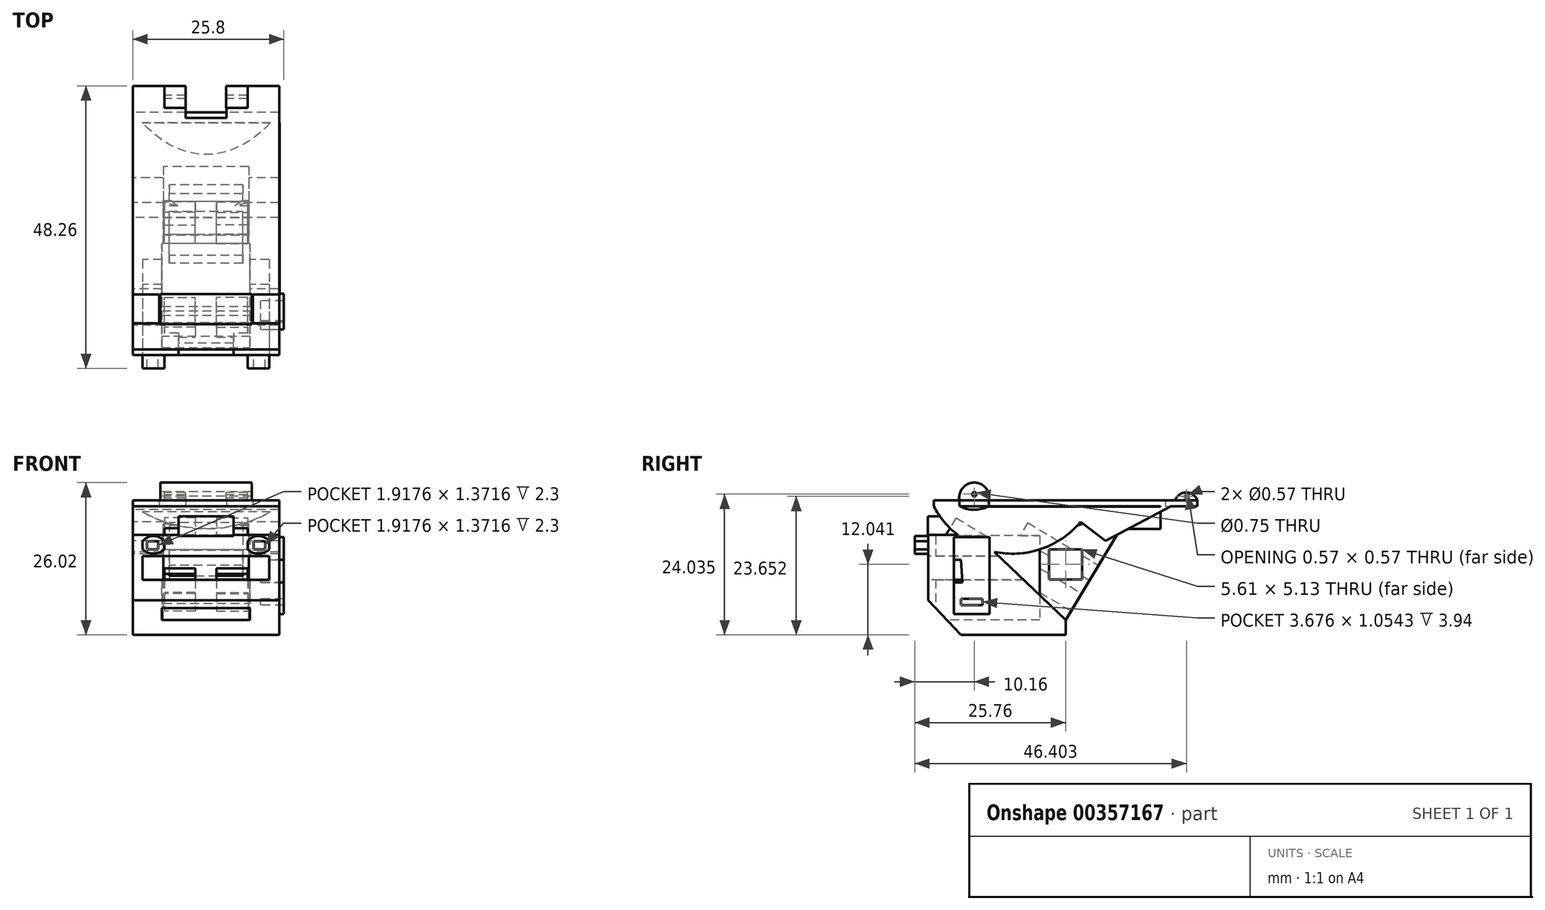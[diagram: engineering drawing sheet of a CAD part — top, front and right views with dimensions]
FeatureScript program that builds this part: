
annotation { "Feature Type Name" : "Feature", "Feature Type Description" : "" }
export const myFeature = defineFeature(function(context is Context, id is Id, definition is map)
    precondition{}
    {
        {
            var Q0;
            Q0=qCreatedBy(makeId("Top.planeOp"),FACE);
            var sketch = newSketch(context, id + "F0", { "sketchPlane" : qUnion([Q0])});
            skLineSegment(sketch, "E0.bottom", {"start": v(12.5, -22.5) * mm, "end": v(-12.5, -22.5) * mm});
            skLineSegment(sketch, "E0.top", {"start": v(12.5, 22.5) * mm, "end": v(3.5, 22.5) * mm});
            skLineSegment(sketch, "E0.left", {"start": v(12.5, -22.5) * mm, "end": v(12.5, -18.1) * mm});
            skLineSegment(sketch, "E0.right", {"start": v(-12.5, -22.5) * mm, "end": v(-12.5, -18.1) * mm});
            skPoint(sketch, "E0.middle", {"position": v(0, 0) * mm});
            skLineSegment(sketch, "E1.MirrorCS", {"start": v(-12.5, -13.1) * mm, "end": v(-8, -13.1) * mm});
            skLineSegment(sketch, "E2.MirrorCS", {"start": v(-8, -13.1) * mm, "end": v(-8, -18.1) * mm});
            skLineSegment(sketch, "E3.MirrorCS", {"start": v(-12.5, -18.1) * mm, "end": v(-8, -18.1) * mm});
            skLineSegment(sketch, "E4.MirrorCS", {"start": v(12.5, -18.1) * mm, "end": v(8, -18.1) * mm});
            skLineSegment(sketch, "E5.MirrorCS", {"start": v(12.5, -13.1) * mm, "end": v(8, -13.1) * mm});
            skLineSegment(sketch, "E6.MirrorCS", {"start": v(8, -13.1) * mm, "end": v(8, -18.1) * mm});
            skLineSegment(sketch, "E7.trimOffspring", {"start": v(-12.5, 18.1) * mm, "end": v(-12.5, 22.5) * mm});
            skLineSegment(sketch, "E8.trimOffspring", {"start": v(12.5, 18.1) * mm, "end": v(12.5, 22.5) * mm});
            skLineSegment(sketch, "E9.trimOffspring", {"start": v(12.5, -13.1) * mm, "end": v(12.5, 13.1) * mm});
            skLineSegment(sketch, "E10.trimOffspring", {"start": v(-12.5, -13.1) * mm, "end": v(-12.5, 13.1) * mm});
            skLineSegment(sketch, "E11", {"start": v(-12.5, 18.1) * mm, "end": v(-12.5, 13.1) * mm});
            skLineSegment(sketch, "E12", {"start": v(12.5, 18.1) * mm, "end": v(12.5, 13.1) * mm});
            skLineSegment(sketch, "E13.bottom", {"start": v(3.5, 17.07) * mm, "end": v(-3.5, 17.07) * mm});
            skLineSegment(sketch, "E13.left", {"start": v(3.5, 17.07) * mm, "end": v(3.5, 22.5) * mm});
            skLineSegment(sketch, "E13.right", {"start": v(-3.5, 17.07) * mm, "end": v(-3.5, 22.5) * mm});
            skPoint(sketch, "E13.middle", {"position": v(0, 22.5) * mm});
            skPoint(sketch, "E14.orphan", {"position": v(-3.5, 27.93) * mm});
            skPoint(sketch, "E15.orphan", {"position": v(3.5, 27.93) * mm});
            skLineSegment(sketch, "E16.trimOffspring", {"start": v(-3.5, 22.5) * mm, "end": v(-12.5, 22.5) * mm});
            skSolve(sketch);
        }
        {
            var Q0;
            Q0 = qSketchRegion(id + "F0", true);
            extrude(context, id + "F1", {"entities" : qUnion([Q0]), "depth" : 1 * mm});
        }
        {
            var Q0;
            Q0=qCreatedBy(makeId("Right.planeOp"),FACE);
            var sketch = newSketch(context, id + "F2", { "sketchPlane" : qUnion([Q0])});
            skCircle(sketch, "E17", {"center": v(-15.6, 2.05) * mm, "radius": 0.38 * mm});
            skLineSegment(sketch, "E18", {"start": v(-18.13, 1) * mm, "end": v(-13.1, 0.97) * mm});
            skArc(sketch, "E19", {"start": v(-13.1, 0.97) * mm, "mid": v(-15.59, 4.04) * mm, "end": v(-18.13, 1) * mm});
            skSolve(sketch);
        }
        {
            var Q0;
            Q0 = qSketchRegion(id + "F2", true);
            extrude(context, id + "F3", {"entities" : qUnion([Q0]), "operationType" : NewBodyOperationType.ADD, "endBound" : BoundingType.SYMMETRIC, "depth" : 15.6 * mm});
        }
        {
            var Q0;
            Q0=qCreatedBy(makeId("Right.planeOp"),FACE);
            var sketch = newSketch(context, id + "F4", { "sketchPlane" : qUnion([Q0])});
            skArc(sketch, "E20", {"start": v(22.5, 1) * mm, "mid": v(20.61, 2.34) * mm, "end": v(18.73, 1) * mm});
            skLineSegment(sketch, "E21", {"start": v(22.5, 1) * mm, "end": v(18.73, 1) * mm});
            skCircle(sketch, "E22", {"center": v(20.64, 1.67) * mm, "radius": 0.28 * mm});
            skSolve(sketch);
        }
        {
            var Q0;
            Q0 = qSketchRegion(id + "F4", true);
            extrude(context, id + "F5", {"entities" : qUnion([Q0]), "endBound" : BoundingType.SYMMETRIC, "depth" : 14.2 * mm});
        }
        {
            var Q0;
            Q0=makeQuery(id+"F5.opExtrude","SWEPT_FACE",FACE,{"disambiguationData":[OSD([sQuery(id+"F4.wireOp",EDGE,"E21")])]});
            var sketch = newSketch(context, id + "F6", { "sketchPlane" : qUnion([Q0])});
            skLineSegment(sketch, "E23.bottom", {"start": v(-3.5, -18.73) * mm, "end": v(3.46, -18.73) * mm});
            skLineSegment(sketch, "E23.top", {"start": v(-3.5, -22.5) * mm, "end": v(3.46, -22.5) * mm});
            skLineSegment(sketch, "E23.left", {"start": v(-3.5, -18.73) * mm, "end": v(-3.5, -22.5) * mm});
            skLineSegment(sketch, "E23.right", {"start": v(3.46, -18.73) * mm, "end": v(3.46, -22.5) * mm});
            skSolve(sketch);
        }
        {
            var Q0;
            Q0=makeQuery(id+"F6.imprint","IMPRINT",FACE,{"disambiguationData":[TD([[makeQuery(id+"F6.imprint","IMPRINT",EDGE,{"derivedFrom":sQuery(id+"F6.wireOp",EDGE,"E23.bottom")}),1.0]])]});
            extrude(context, id + "F7", {"entities" : qUnion([Q0]), "operationType" : NewBodyOperationType.REMOVE, "oppositeDirection" : true, "depth" : 25 * mm});
        }
        {
            var Q0;
            Q0=qCreatedBy(makeId("Right.planeOp"),FACE);
            var sketch = newSketch(context, id + "F8", { "sketchPlane" : qUnion([Q0])});
            skLineSegment(sketch, "E24", {"start": v(18.02, 0) * mm, "end": v(6.85, -5.94) * mm});
            skLineSegment(sketch, "E25", {"start": v(6.85, -5.94) * mm, "end": v(2.57, -2.68) * mm});
            skArc(sketch, "E26", {"start": v(-22.53, 0) * mm, "mid": v(-10.7, -8.04) * mm, "end": v(2.57, -2.68) * mm});
            skLineSegment(sketch, "E27", {"start": v(-22.53, 0) * mm, "end": v(0, 0) * mm});
            skLineSegment(sketch, "E28", {"start": v(0, 0) * mm, "end": v(18.02, 0) * mm});
            skSolve(sketch);
        }
        {
            var Q0;
            Q0=qCreatedBy(makeId("Front.planeOp"),FACE);
            var sketch = newSketch(context, id + "F9", { "sketchPlane" : qUnion([Q0])});
            skArc(sketch, "E29", {"start": v(-12.45, 0) * mm, "mid": v(0.07, -3.86) * mm, "end": v(12.6, 0) * mm});
            skLineSegment(sketch, "E30", {"start": v(-12.45, 0) * mm, "end": v(12.6, 0) * mm});
            skSolve(sketch);
        }
        {
            var Q0;
            Q0 = qSketchRegion(id + "F8", true);
            extrude(context, id + "F10", {"entities" : qUnion([Q0]), "operationType" : NewBodyOperationType.ADD, "endBound" : BoundingType.SYMMETRIC, "depth" : 25 * mm});
        }
        {
            var Q0;
            Q0 = qSketchRegion(id + "F9", true);
            extrude(context, id + "F11", {"entities" : qUnion([Q0]), "operationType" : NewBodyOperationType.ADD, "endBound" : BoundingType.SYMMETRIC, "depth" : 32.4 * mm});
        }
        {
            var Q0;
            Q0=qCreatedBy(makeId("Right.planeOp"),FACE);
            var sketch = newSketch(context, id + "F12", { "sketchPlane" : qUnion([Q0])});
            skLineSegment(sketch, "E31", {"start": v(11.72, 0) * mm, "end": v(0, -19.43) * mm});
            skLineSegment(sketch, "E32", {"start": v(0, -19.43) * mm, "end": v(-11.93, -8.08) * mm});
            skLineSegment(sketch, "E33", {"start": v(-11.93, -8.08) * mm, "end": v(11.72, 0) * mm});
            skLineSegment(sketch, "E34.bottom", {"start": v(2.8, -7.37) * mm, "end": v(-2.8, -7.37) * mm});
            skLineSegment(sketch, "E34.top", {"start": v(2.8, -12.5) * mm, "end": v(-2.8, -12.5) * mm});
            skLineSegment(sketch, "E34.left", {"start": v(2.8, -7.37) * mm, "end": v(2.8, -12.5) * mm});
            skLineSegment(sketch, "E34.right", {"start": v(-2.8, -7.37) * mm, "end": v(-2.8, -12.5) * mm});
            skPoint(sketch, "E34.middle", {"position": v(0, -9.94) * mm});
            skSolve(sketch);
        }
        {
            var Q0;
            Q0=makeQuery(id+"F12.imprint","IMPRINT",FACE,{"disambiguationData":[TD([[makeQuery(id+"F12.imprint","IMPRINT",EDGE,{"derivedFrom":sQuery(id+"F12.wireOp",EDGE,"E31")}),-1.0]])]});
            var Q1;
            Q1=makeQuery(id+"F12.imprint","IMPRINT",FACE,{"disambiguationData":[TD([[makeQuery(id+"F12.imprint","IMPRINT",EDGE,{"derivedFrom":sQuery(id+"F12.wireOp",EDGE,"EPClmVz8-GrpX-KQZJ-WgSQ-VfGSgsv4AABU")}),1.0]])]});
            var Q2;
            {var subQ0=sQuery(id+"F12.wireOp",EDGE,"xVboNKFk-sm6J-4G5X-BPrH-lB6fLDyY1mAe");Q2=makeQuery(id+"F12.imprint","IMPRINT",FACE,{"disambiguationData":[TD([[makeQuery(id+"F12.imprint","IMPRINT",EDGE,{"derivedFrom":subQ0}),1.0]])]});}
            var Q3;
            {var subQ0=sQuery(id+"F12.wireOp",EDGE,"dIe3VIoE-PewE-ehZx-6Q2n-xNr1zAI1dDmG");Q3=makeQuery(id+"F12.imprint","IMPRINT",FACE,{"disambiguationData":[TD([[makeQuery(id+"F12.imprint","IMPRINT",EDGE,{"derivedFrom":subQ0}),-1.0]])]});}
            var Q4;
            Q4=makeQuery(id+"F12.imprint","IMPRINT",FACE,{"disambiguationData":[TD([[makeQuery(id+"F12.imprint","IMPRINT",EDGE,{"derivedFrom":sQuery(id+"F12.wireOp",EDGE,"3RO27YDa-2lhc-6LYU-8um3-BjFFgWLBZsGJ.bottom")}),-1.0]])]});
            var Q5;
            Q5=makeQuery(id+"F12.imprint","IMPRINT",FACE,{"disambiguationData":[TD([[makeQuery(id+"F12.imprint","IMPRINT",EDGE,{"derivedFrom":sQuery(id+"F12.wireOp",EDGE,"KlLquwEu-1y5j-Y41z-U9SY-rjszHWDUEvhw.bottom")}),1.0]])]});
            extrude(context, id + "F13", {"entities" : qUnion([Q0, Q1, Q2, Q3, Q4, Q5]), "operationType" : NewBodyOperationType.ADD, "endBound" : BoundingType.SYMMETRIC, "oppositeDirection" : true, "depth" : 14.6 * mm});
        }
        {
            var Q0;
            Q0=qCreatedBy(makeId("Front.planeOp"),FACE);
            var sketch = newSketch(context, id + "F14", { "sketchPlane" : qUnion([Q0])});
            skLineSegment(sketch, "E35.bottom", {"start": v(4.7, -5.1) * mm, "end": v(-4.7, -5.1) * mm});
            skLineSegment(sketch, "E35.top", {"start": v(4.7, -1.73) * mm, "end": v(-4.7, -1.73) * mm});
            skLineSegment(sketch, "E35.left", {"start": v(4.7, -5.1) * mm, "end": v(4.7, -1.73) * mm});
            skLineSegment(sketch, "E35.right", {"start": v(-4.7, -5.1) * mm, "end": v(-4.7, -1.73) * mm});
            skPoint(sketch, "E35.middle", {"position": v(0, -3.41) * mm});
            skLineSegment(sketch, "E36", {"start": v(-4.7, -1.73) * mm, "end": v(-2.31, -5.1) * mm});
            skLineSegment(sketch, "E37", {"start": v(-2.31, -5.1) * mm, "end": v(0, -3.41) * mm});
            skLineSegment(sketch, "E38", {"start": v(0, -3.41) * mm, "end": v(2.21, -5.1) * mm});
            skLineSegment(sketch, "E39", {"start": v(2.21, -5.1) * mm, "end": v(4.7, -1.73) * mm});
            skLineSegment(sketch, "E40", {"start": v(-4.7, -1.73) * mm, "end": v(4.7, -1.73) * mm});
            skSolve(sketch);
        }
        {
            var Q0;
            Q0 = qSketchRegion(id + "F14", true);
            extrude(context, id + "F15", {"entities" : qUnion([Q0]), "operationType" : NewBodyOperationType.ADD, "depth" : 23.5 * mm});
        }
        {
            var Q0;
            Q0=makeQuery(id+"F13.opExtrude","SWEPT_FACE",FACE,{"disambiguationData":[OSD([sQuery(id+"F12.wireOp",EDGE,"E31")])]});
            var sketch = newSketch(context, id + "F16", { "sketchPlane" : qUnion([Q0])});
            skLineSegment(sketch, "E41.bottom", {"start": v(1.82, -11.36) * mm, "end": v(7.1, -11.36) * mm});
            skLineSegment(sketch, "E41.top", {"start": v(1.82, -14.87) * mm, "end": v(7.1, -14.87) * mm});
            skLineSegment(sketch, "E41.left", {"start": v(1.82, -11.36) * mm, "end": v(1.82, -14.87) * mm});
            skLineSegment(sketch, "E41.right", {"start": v(7.1, -11.36) * mm, "end": v(7.1, -14.87) * mm});
            skPoint(sketch, "E41.middle", {"position": v(4.46, -13.12) * mm});
            skLineSegment(sketch, "E42.MirrorCS", {"start": v(-1.82, -11.36) * mm, "end": v(-7.1, -11.36) * mm});
            skLineSegment(sketch, "E43.MirrorCS", {"start": v(-1.82, -14.87) * mm, "end": v(-7.1, -14.87) * mm});
            skLineSegment(sketch, "E44.MirrorCS", {"start": v(-1.82, -11.36) * mm, "end": v(-1.82, -14.87) * mm});
            skLineSegment(sketch, "E45.MirrorCS", {"start": v(-7.1, -11.36) * mm, "end": v(-7.1, -14.87) * mm});
            skSolve(sketch);
        }
        {
            var Q0;
            Q0 = qSketchRegion(id + "F16", true);
            extrude(context, id + "F17", {"entities" : qUnion([Q0]), "operationType" : NewBodyOperationType.REMOVE, "oppositeDirection" : true, "depth" : 25 * mm});
        }
        {
            var Q0;
            Q0=qCreatedBy(makeId("Right.planeOp"),FACE);
            var sketch = newSketch(context, id + "F18", { "sketchPlane" : qUnion([Q0])});
            skArc(sketch, "E46", {"start": v(-18.06, 0) * mm, "mid": v(-15.6, -0.62) * mm, "end": v(-13.13, 0) * mm});
            skLineSegment(sketch, "E47", {"start": v(-13.13, 0) * mm, "end": v(-18.06, 0) * mm});
            skSolve(sketch);
        }
        {
            var Q0;
            Q0 = qSketchRegion(id + "F18", true);
            extrude(context, id + "F19", {"entities" : qUnion([Q0]), "operationType" : NewBodyOperationType.REMOVE, "endBound" : BoundingType.SYMMETRIC, "depth" : 29.26 * mm});
        }
        {
            var Q0;
            Q0=makeQuery(id+"F13.opExtrude","SWEPT_FACE",FACE,{"disambiguationData":[OSD([sQuery(id+"F12.wireOp",EDGE,"E31")])]});
            var sketch = newSketch(context, id + "F20", { "sketchPlane" : qUnion([Q0])});
            skLineSegment(sketch, "E48.bottom", {"start": v(-6.28, -5.73) * mm, "end": v(6.28, -5.73) * mm});
            skLineSegment(sketch, "E48.top", {"start": v(-6.28, -8.73) * mm, "end": v(6.28, -8.73) * mm});
            skLineSegment(sketch, "E48.left", {"start": v(-6.28, -5.73) * mm, "end": v(-6.28, -8.73) * mm});
            skLineSegment(sketch, "E48.right", {"start": v(6.28, -5.73) * mm, "end": v(6.28, -8.73) * mm});
            skPoint(sketch, "E48.middle", {"position": v(0, -7.23) * mm});
            skSolve(sketch);
        }
        {
            var Q0;
            Q0 = qSketchRegion(id + "F20", true);
            extrude(context, id + "F21", {"entities" : qUnion([Q0]), "operationType" : NewBodyOperationType.REMOVE, "oppositeDirection" : true, "depth" : 14.1 * mm});
        }
        {
            var Q0;
            Q0=qCreatedBy(makeId("Right.planeOp"),FACE);
            var sketch = newSketch(context, id + "F22", { "sketchPlane" : qUnion([Q0])});
            skLineSegment(sketch, "E49", {"start": v(0, -19.45) * mm, "end": v(-23.46, -19.45) * mm});
            skLineSegment(sketch, "E50", {"start": v(-23.46, -19.45) * mm, "end": v(-23.46, -4.93) * mm});
            skLineSegment(sketch, "E51", {"start": v(-23.46, -4.93) * mm, "end": v(-18.28, -4.93) * mm});
            skLineSegment(sketch, "E52", {"start": v(-18.28, -4.93) * mm, "end": v(-12.14, -7.83) * mm});
            skLineSegment(sketch, "E53", {"start": v(0, -19.45) * mm, "end": v(-12.14, -7.83) * mm});
            skSolve(sketch);
        }
        {
            var Q0;
            Q0 = qSketchRegion(id + "F22", true);
            extrude(context, id + "F23", {"entities" : qUnion([Q0]), "operationType" : NewBodyOperationType.ADD, "endBound" : BoundingType.SYMMETRIC, "depth" : 25 * mm});
        }
        {
            var Q0;
            Q0=makeQuery(id+"F23.opExtrude","SWEPT_FACE",FACE,{"disambiguationData":[OSD([sQuery(id+"F22.wireOp",EDGE,"E50")])]});
            var sketch = newSketch(context, id + "F24", { "sketchPlane" : qUnion([Q0])});
            skLineSegment(sketch, "E54.bottom", {"start": v(10.81, -12.58) * mm, "end": v(-10.81, -12.58) * mm});
            skLineSegment(sketch, "E54.top", {"start": v(10.81, -8.5) * mm, "end": v(-10.81, -8.5) * mm});
            skLineSegment(sketch, "E54.left", {"start": v(10.81, -12.58) * mm, "end": v(10.81, -8.5) * mm});
            skLineSegment(sketch, "E54.right", {"start": v(-10.81, -12.58) * mm, "end": v(-10.81, -8.5) * mm});
            skPoint(sketch, "E54.middle", {"position": v(0, -10.54) * mm});
            skSolve(sketch);
        }
        {
            var Q0;
            Q0=makeQuery(id+"F24.imprint","IMPRINT",FACE,{"disambiguationData":[TD([[makeQuery(id+"F24.imprint","IMPRINT",EDGE,{"derivedFrom":sQuery(id+"F24.wireOp",EDGE,"E54.bottom")}),-1.0]])]});
            extrude(context, id + "F25", {"entities" : qUnion([Q0]), "operationType" : NewBodyOperationType.REMOVE, "oppositeDirection" : true, "depth" : 18 * mm});
        }
        {
            var Q0;
            Q0=makeQuery(id+"F23.opExtrude","SWEPT_FACE",FACE,{"disambiguationData":[OSD([sQuery(id+"F22.wireOp",EDGE,"E49")])]});
            var sketch = newSketch(context, id + "F26", { "sketchPlane" : qUnion([Q0])});
            skLineSegment(sketch, "E55.bottom", {"start": v(7.52, 4.4) * mm, "end": v(-7.52, 4.4) * mm});
            skLineSegment(sketch, "E55.top", {"start": v(7.52, 22.22) * mm, "end": v(-7.52, 22.22) * mm});
            skLineSegment(sketch, "E55.left", {"start": v(7.52, 4.4) * mm, "end": v(7.52, 22.22) * mm});
            skLineSegment(sketch, "E55.right", {"start": v(-7.52, 4.4) * mm, "end": v(-7.52, 22.22) * mm});
            skPoint(sketch, "E55.middle", {"position": v(0, 13.3) * mm});
            skSolve(sketch);
        }
        {
            var Q0;
            Q0 = qSketchRegion(id + "F26", true);
            extrude(context, id + "F27", {"entities" : qUnion([Q0]), "operationType" : NewBodyOperationType.REMOVE, "oppositeDirection" : true, "depth" : 14.4 * mm});
        }
        {
            var Q0;
            Q0=makeQuery(id+"F23.boolean.opBoolean","MERGE",FACE,{"derivedFrom":[makeQuery(id+"F10.boolean.opBoolean","MERGE",FACE,{"derivedFrom":[makeQuery(id+"F1.opExtrude","SWEPT_FACE",FACE,{"disambiguationData":[OSD([sQuery(id+"F0.wireOp",EDGE,"E0.left")])]}),makeQuery(id+"F1.opExtrude","SWEPT_FACE",FACE,{"disambiguationData":[OSD([sQuery(id+"F0.wireOp",EDGE,"E8.trimOffspring"),sQuery(id+"F0.wireOp",EDGE,"E9.trimOffspring"),sQuery(id+"F0.wireOp",EDGE,"E12")])]}),makeQuery(id+"F10.opExtrude","CAP_FACE",FACE,{"disambiguationData":[OSD([sQuery(id+"F8.wireOp",EDGE,"E24"),sQuery(id+"F8.wireOp",EDGE,"E25"),sQuery(id+"F8.wireOp",EDGE,"E26"),sQuery(id+"F8.wireOp",EDGE,"E27"),sQuery(id+"F8.wireOp",EDGE,"E28")])],"isStart":false})]}),makeQuery(id+"F23.opExtrude","CAP_FACE",FACE,{"disambiguationData":[OSD([sQuery(id+"F22.wireOp",EDGE,"E49"),sQuery(id+"F22.wireOp",EDGE,"E50"),sQuery(id+"F22.wireOp",EDGE,"E51"),sQuery(id+"F22.wireOp",EDGE,"E52"),sQuery(id+"F22.wireOp",EDGE,"E53")])],"isStart":false})]});
            var sketch = newSketch(context, id + "F28", { "sketchPlane" : qUnion([Q0])});
            skLineSegment(sketch, "E56", {"start": v(-23.46, -19.45) * mm, "end": v(0, -19.45) * mm});
            skLineSegment(sketch, "E57", {"start": v(-23.46, -19.45) * mm, "end": v(-23.46, -24.5) * mm});
            skLineSegment(sketch, "E58", {"start": v(-23.46, -24.5) * mm, "end": v(0, -24.5) * mm});
            skLineSegment(sketch, "E59", {"start": v(0, -24.5) * mm, "end": v(0, -19.45) * mm});
            skSolve(sketch);
        }
        {
            var Q0;
            Q0 = qSketchRegion(id + "F28", true);
            extrude(context, id + "F29", {"entities" : qUnion([Q0]), "operationType" : NewBodyOperationType.ADD, "oppositeDirection" : true, "depth" : 25 * mm});
        }
        {
            var Q0;
            Q0=makeQuery(id+"F29.boolean.opBoolean","MERGE",FACE,{"derivedFrom":[makeQuery(id+"F23.boolean.opBoolean","MERGE",FACE,{"derivedFrom":[makeQuery(id+"F10.boolean.opBoolean","MERGE",FACE,{"derivedFrom":[makeQuery(id+"F1.opExtrude","SWEPT_FACE",FACE,{"disambiguationData":[OSD([sQuery(id+"F0.wireOp",EDGE,"E0.right")])]}),makeQuery(id+"F1.opExtrude","SWEPT_FACE",FACE,{"disambiguationData":[OSD([sQuery(id+"F0.wireOp",EDGE,"E7.trimOffspring"),sQuery(id+"F0.wireOp",EDGE,"E10.trimOffspring"),sQuery(id+"F0.wireOp",EDGE,"E11")])]}),makeQuery(id+"F10.opExtrude","CAP_FACE",FACE,{"disambiguationData":[OSD([sQuery(id+"F8.wireOp",EDGE,"E24"),sQuery(id+"F8.wireOp",EDGE,"E25"),sQuery(id+"F8.wireOp",EDGE,"E26"),sQuery(id+"F8.wireOp",EDGE,"E27"),sQuery(id+"F8.wireOp",EDGE,"E28")])],"isStart":true})]}),makeQuery(id+"F23.opExtrude","CAP_FACE",FACE,{"disambiguationData":[OSD([sQuery(id+"F22.wireOp",EDGE,"E49"),sQuery(id+"F22.wireOp",EDGE,"E50"),sQuery(id+"F22.wireOp",EDGE,"E51"),sQuery(id+"F22.wireOp",EDGE,"E52"),sQuery(id+"F22.wireOp",EDGE,"E53")])],"isStart":true})]}),makeQuery(id+"F29.opExtrude","CAP_FACE",FACE,{"disambiguationData":[OSD([sQuery(id+"F28.wireOp",EDGE,"E56"),sQuery(id+"F28.wireOp",EDGE,"E57"),sQuery(id+"F28.wireOp",EDGE,"E58"),sQuery(id+"F28.wireOp",EDGE,"E59")])],"isStart":false})]});
            var sketch = newSketch(context, id + "F30", { "sketchPlane" : qUnion([Q0])});
            skLineSegment(sketch, "E60", {"start": v(23.46, -16.09) * mm, "end": v(15.48, -24.5) * mm});
            skLineSegment(sketch, "E61", {"start": v(23.46, -16.93) * mm, "end": v(23.46, -24.5) * mm});
            skLineSegment(sketch, "E62", {"start": v(23.46, -24.5) * mm, "end": v(15.48, -24.5) * mm});
            skSolve(sketch);
        }
        {
            var Q0;
            Q0 = qSketchRegion(id + "F30", true);
            var Q1;
            {var subQ0=sQuery(id+"F30.wireOp",EDGE,"E60");Q1=makeQuery(id+"F30.imprint","IMPRINT",FACE,{"disambiguationData":[TD([[makeQuery(id+"F30.imprint","IMPRINT",EDGE,{"derivedFrom":subQ0}),1.0]])]});}
            extrude(context, id + "F31", {"entities" : qUnion([Q0, Q1]), "operationType" : NewBodyOperationType.REMOVE, "oppositeDirection" : true, "depth" : 25 * mm});
        }
        {
            var Q0;
            Q0=makeQuery(id+"F29.boolean.opBoolean","MERGE",FACE,{"derivedFrom":[makeQuery(id+"F23.opExtrude","SWEPT_FACE",FACE,{"disambiguationData":[OSD([sQuery(id+"F22.wireOp",EDGE,"E50")])]}),makeQuery(id+"F29.opExtrude","SWEPT_FACE",FACE,{"disambiguationData":[OSD([sQuery(id+"F28.wireOp",EDGE,"E57")])]})]});
            var sketch = newSketch(context, id + "F32", { "sketchPlane" : qUnion([Q0])});
            skLineSegment(sketch, "E63.bottom", {"start": v(-10.81, -6.01) * mm, "end": v(-7.1, -6.01) * mm});
            skLineSegment(sketch, "E63.top", {"start": v(-10.81, -7.39) * mm, "end": v(-7.1, -7.39) * mm});
            skLineSegment(sketch, "E63.left", {"start": v(-10.81, -6.01) * mm, "end": v(-10.81, -7.39) * mm});
            skLineSegment(sketch, "E63.right", {"start": v(-7.1, -6.01) * mm, "end": v(-7.1, -7.39) * mm});
            skLineSegment(sketch, "E64.MirrorCS", {"start": v(10.81, -6.01) * mm, "end": v(7.1, -6.01) * mm});
            skLineSegment(sketch, "E65.MirrorCS", {"start": v(10.81, -6.01) * mm, "end": v(10.81, -7.39) * mm});
            skLineSegment(sketch, "E66.MirrorCS", {"start": v(7.1, -6.01) * mm, "end": v(7.1, -7.39) * mm});
            skArc(sketch, "E67", {"start": v(7.1, -7.39) * mm, "mid": v(8.96, -8.12) * mm, "end": v(10.81, -7.39) * mm});
            skLineSegment(sketch, "E68", {"start": v(10.1, -7.88) * mm, "end": v(10.1, -6.01) * mm});
            skLineSegment(sketch, "E69", {"start": v(8.17, -8) * mm, "end": v(8.17, -6.01) * mm});
            skLineSegment(sketch, "E70", {"start": v(10.1, -7.88) * mm, "end": v(8.17, -8) * mm});
            skArc(sketch, "E71.MirrorCS", {"start": v(-7.1, -7.39) * mm, "mid": v(-8.96, -8.12) * mm, "end": v(-10.81, -7.39) * mm});
            skLineSegment(sketch, "E72.MirrorCS", {"start": v(-8.17, -8) * mm, "end": v(-8.17, -6.01) * mm});
            skLineSegment(sketch, "E73.MirrorCS", {"start": v(-10.1, -7.88) * mm, "end": v(-10.1, -6.01) * mm});
            skLineSegment(sketch, "E74.MirrorCS", {"start": v(-10.1, -7.88) * mm, "end": v(-8.17, -8) * mm});
            skArc(sketch, "E75", {"start": v(-7.1, -6.01) * mm, "mid": v(-8.96, -5.08) * mm, "end": v(-10.81, -6.01) * mm});
            skArc(sketch, "E76", {"start": v(10.81, -6.01) * mm, "mid": v(8.96, -5.43) * mm, "end": v(7.1, -6.01) * mm});
            skLineSegment(sketch, "E77.MirrorCS", {"start": v(10.81, -7.39) * mm, "end": v(7.1, -7.39) * mm});
            skArc(sketch, "E78.MirrorCS", {"start": v(7.1, -6.01) * mm, "mid": v(8.96, -5.08) * mm, "end": v(10.81, -6.01) * mm});
            skSolve(sketch);
        }
        {
            var Q0;
            Q0 = qSketchRegion(id + "F32", true);
            extrude(context, id + "F33", {"entities" : qUnion([Q0]), "operationType" : NewBodyOperationType.ADD, "depth" : 2.3 * mm});
        }
        {
            var Q0;
            Q0=makeQuery(id+"F29.boolean.opBoolean","MERGE",FACE,{"derivedFrom":[makeQuery(id+"F23.boolean.opBoolean","MERGE",FACE,{"derivedFrom":[makeQuery(id+"F10.boolean.opBoolean","MERGE",FACE,{"derivedFrom":[makeQuery(id+"F1.opExtrude","SWEPT_FACE",FACE,{"disambiguationData":[OSD([sQuery(id+"F0.wireOp",EDGE,"E0.left")])]}),makeQuery(id+"F1.opExtrude","SWEPT_FACE",FACE,{"disambiguationData":[OSD([sQuery(id+"F0.wireOp",EDGE,"E8.trimOffspring"),sQuery(id+"F0.wireOp",EDGE,"E9.trimOffspring"),sQuery(id+"F0.wireOp",EDGE,"E12")])]}),makeQuery(id+"F10.opExtrude","CAP_FACE",FACE,{"disambiguationData":[OSD([sQuery(id+"F8.wireOp",EDGE,"E24"),sQuery(id+"F8.wireOp",EDGE,"E25"),sQuery(id+"F8.wireOp",EDGE,"E26"),sQuery(id+"F8.wireOp",EDGE,"E27"),sQuery(id+"F8.wireOp",EDGE,"E28")])],"isStart":false})]}),makeQuery(id+"F23.opExtrude","CAP_FACE",FACE,{"disambiguationData":[OSD([sQuery(id+"F22.wireOp",EDGE,"E49"),sQuery(id+"F22.wireOp",EDGE,"E50"),sQuery(id+"F22.wireOp",EDGE,"E51"),sQuery(id+"F22.wireOp",EDGE,"E52"),sQuery(id+"F22.wireOp",EDGE,"E53")])],"isStart":false})]}),makeQuery(id+"F29.opExtrude","CAP_FACE",FACE,{"disambiguationData":[OSD([sQuery(id+"F28.wireOp",EDGE,"E56"),sQuery(id+"F28.wireOp",EDGE,"E57"),sQuery(id+"F28.wireOp",EDGE,"E58"),sQuery(id+"F28.wireOp",EDGE,"E59")])],"isStart":true})]});
            var sketch = newSketch(context, id + "F34", { "sketchPlane" : qUnion([Q0])});
            skLineSegment(sketch, "E79.bottom", {"start": v(-15.48, -24.5) * mm, "end": v(0, -24.5) * mm});
            skLineSegment(sketch, "E79.top", {"start": v(-15.48, -21.98) * mm, "end": v(0, -21.98) * mm});
            skLineSegment(sketch, "E79.right", {"start": v(0, -24.5) * mm, "end": v(0, -21.98) * mm});
            skLineSegment(sketch, "E80", {"start": v(-15.48, -21.98) * mm, "end": v(-17.88, -21.98) * mm});
            skLineSegment(sketch, "E81", {"start": v(-15.48, -24.5) * mm, "end": v(-17.88, -21.98) * mm});
            skSolve(sketch);
        }
        {
            var Q0;
            Q0 = qSketchRegion(id + "F34", true);
            extrude(context, id + "F35", {"entities" : qUnion([Q0]), "operationType" : NewBodyOperationType.REMOVE, "oppositeDirection" : true, "depth" : 25 * mm});
        }
        {
            var Q0;
            Q0 = qSketchRegion(id + "F34", true);
            extrude(context, id + "F36", {"entities" : qUnion([Q0]), "operationType" : NewBodyOperationType.REMOVE, "depth" : 3.9 * mm});
        }
        {
            var Q0;
            Q0=makeQuery(id+"F29.boolean.opBoolean","MERGE",FACE,{"derivedFrom":[makeQuery(id+"F23.boolean.opBoolean","MERGE",FACE,{"derivedFrom":[makeQuery(id+"F10.boolean.opBoolean","MERGE",FACE,{"derivedFrom":[makeQuery(id+"F1.opExtrude","SWEPT_FACE",FACE,{"disambiguationData":[OSD([sQuery(id+"F0.wireOp",EDGE,"E0.left")])]}),makeQuery(id+"F1.opExtrude","SWEPT_FACE",FACE,{"disambiguationData":[OSD([sQuery(id+"F0.wireOp",EDGE,"E8.trimOffspring"),sQuery(id+"F0.wireOp",EDGE,"E9.trimOffspring"),sQuery(id+"F0.wireOp",EDGE,"E12")])]}),makeQuery(id+"F10.opExtrude","CAP_FACE",FACE,{"disambiguationData":[OSD([sQuery(id+"F8.wireOp",EDGE,"E24"),sQuery(id+"F8.wireOp",EDGE,"E25"),sQuery(id+"F8.wireOp",EDGE,"E26"),sQuery(id+"F8.wireOp",EDGE,"E27"),sQuery(id+"F8.wireOp",EDGE,"E28")])],"isStart":false})]}),makeQuery(id+"F23.opExtrude","CAP_FACE",FACE,{"disambiguationData":[OSD([sQuery(id+"F22.wireOp",EDGE,"E49"),sQuery(id+"F22.wireOp",EDGE,"E50"),sQuery(id+"F22.wireOp",EDGE,"E51"),sQuery(id+"F22.wireOp",EDGE,"E52"),sQuery(id+"F22.wireOp",EDGE,"E53")])],"isStart":false})]}),makeQuery(id+"F29.opExtrude","CAP_FACE",FACE,{"disambiguationData":[OSD([sQuery(id+"F28.wireOp",EDGE,"E56"),sQuery(id+"F28.wireOp",EDGE,"E57"),sQuery(id+"F28.wireOp",EDGE,"E58"),sQuery(id+"F28.wireOp",EDGE,"E59")])],"isStart":true})]});
            var sketch = newSketch(context, id + "F37", { "sketchPlane" : qUnion([Q0])});
            skLineSegment(sketch, "E82.bottom", {"start": v(-19.08, -5.31) * mm, "end": v(-12.97, -5.31) * mm});
            skLineSegment(sketch, "E82.top", {"start": v(-19.08, -18.44) * mm, "end": v(-12.97, -18.44) * mm});
            skLineSegment(sketch, "E82.left", {"start": v(-19.08, -5.31) * mm, "end": v(-19.08, -18.44) * mm});
            skLineSegment(sketch, "E82.right", {"start": v(-12.97, -5.31) * mm, "end": v(-12.97, -18.44) * mm});
            skPoint(sketch, "E82.middle", {"position": v(-16.03, -11.88) * mm});
            skLineSegment(sketch, "E83", {"start": v(-19.08, -13.06) * mm, "end": v(-17.62, -13.06) * mm});
            skLineSegment(sketch, "E84", {"start": v(-17.62, -13.06) * mm, "end": v(-17.88, -9.16) * mm});
            skLineSegment(sketch, "E85", {"start": v(-17.88, -9.16) * mm, "end": v(-19.08, -9.16) * mm});
            skLineSegment(sketch, "E86.bottom", {"start": v(-18.48, -6.4) * mm, "end": v(-13.57, -6.4) * mm});
            skLineSegment(sketch, "E86.top", {"start": v(-18.48, -17.35) * mm, "end": v(-13.57, -17.35) * mm});
            skLineSegment(sketch, "E86.left", {"start": v(-18.48, -6.4) * mm, "end": v(-18.48, -9.16) * mm});
            skLineSegment(sketch, "E86.right", {"start": v(-13.57, -6.4) * mm, "end": v(-13.57, -17.35) * mm});
            skLineSegment(sketch, "E87.trimOffspring", {"start": v(-18.48, -13.06) * mm, "end": v(-18.48, -17.35) * mm});
            skLineSegment(sketch, "E88.bottom", {"start": v(-17.88, -16.89) * mm, "end": v(-14.2, -16.89) * mm});
            skLineSegment(sketch, "E88.top", {"start": v(-17.88, -15.83) * mm, "end": v(-14.2, -15.83) * mm});
            skLineSegment(sketch, "E88.left", {"start": v(-17.88, -16.89) * mm, "end": v(-17.88, -15.83) * mm});
            skLineSegment(sketch, "E88.right", {"start": v(-14.2, -16.89) * mm, "end": v(-14.2, -15.83) * mm});
            skPoint(sketch, "E88.middle", {"position": v(-16.05, -16.36) * mm});
            skSolve(sketch);
        }
        {
            var Q0;
            {var subQ1=sQuery(id+"F37.wireOp",EDGE,"E84");Q0=makeQuery(id+"F37.imprint","IMPRINT",FACE,{"disambiguationData":[TD([[makeQuery(id+"F37.imprint","IMPRINT",EDGE,{"derivedFrom":subQ1}),-1.0]])]});}
            var Q1;
            {var subQ7=sQuery(id+"F37.wireOp",EDGE,"E82.bottom");Q1=makeQuery(id+"F37.imprint","IMPRINT",FACE,{"disambiguationData":[TD([[makeQuery(id+"F37.imprint","IMPRINT",EDGE,{"derivedFrom":subQ7}),-1.0]])]});}
            extrude(context, id + "F38", {"entities" : qUnion([Q0, Q1]), "operationType" : NewBodyOperationType.ADD, "depth" : 0.8 * mm});
        }
        {
            var Q0;
            {var subQ0=sQuery(id+"F37.wireOp",EDGE,"E84");Q0=makeQuery(id+"F37.imprint","IMPRINT",FACE,{"disambiguationData":[TD([[makeQuery(id+"F37.imprint","IMPRINT",EDGE,{"derivedFrom":subQ0}),1.0]])]});}
            var Q1;
            Q1=makeQuery(id+"F37.imprint","IMPRINT",FACE,{"disambiguationData":[TD([[makeQuery(id+"F37.imprint","IMPRINT",EDGE,{"derivedFrom":sQuery(id+"F37.wireOp",EDGE,"E88.bottom")}),1.0]])]});
            extrude(context, id + "F39", {"entities" : qUnion([Q0, Q1]), "operationType" : NewBodyOperationType.REMOVE, "oppositeDirection" : true, "depth" : 3.14 * mm});
        }
    });
